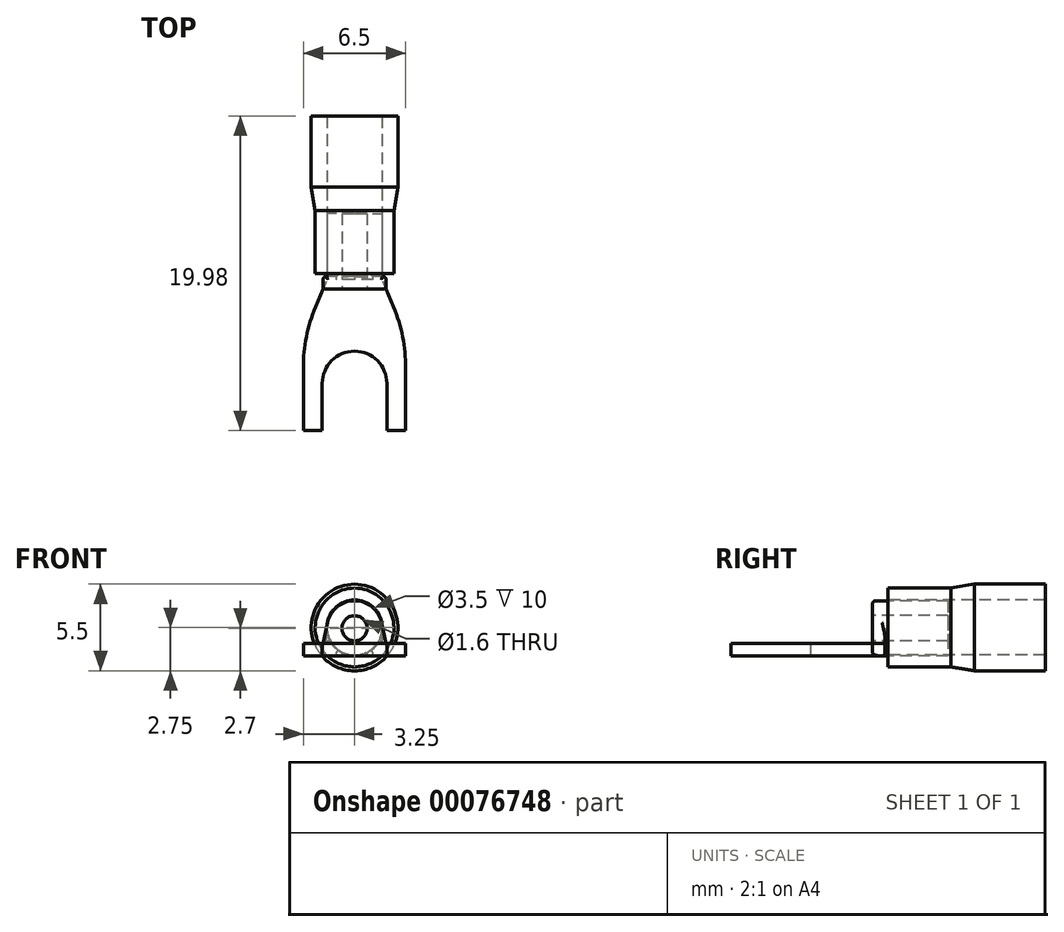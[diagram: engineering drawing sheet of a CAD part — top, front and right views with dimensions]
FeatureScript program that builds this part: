
annotation { "Feature Type Name" : "Feature", "Feature Type Description" : "" }
export const myFeature = defineFeature(function(context is Context, id is Id, definition is map)
    precondition{}
    {
        {
            var Q0;
            Q0=qCreatedBy(makeId("Top.planeOp"),FACE);
            var sketch = newSketch(context, id + "F0", { "sketchPlane" : qUnion([Q0])});
            skLineSegment(sketch, "E0.bottom", {"start": v(2, 4.52) * mm, "end": v(-2, 4.52) * mm});
            skLineSegment(sketch, "E0.top", {"start": v(3.25, -4.48) * mm, "end": v(2.05, -4.48) * mm});
            skLineSegment(sketch, "E0.left", {"start": v(3.25, -0.48) * mm, "end": v(3.25, -4.48) * mm});
            skLineSegment(sketch, "E0.right", {"start": v(-3.25, -0.48) * mm, "end": v(-3.25, -4.48) * mm});
            skPoint(sketch, "E0.middle", {"position": v(0, 0) * mm});
            skLineSegment(sketch, "E1", {"start": v(2.05, -4.48) * mm, "end": v(2.05, -1.48) * mm});
            skLineSegment(sketch, "E2", {"start": v(-2.05, -4.48) * mm, "end": v(-2.05, -1.48) * mm});
            skArc(sketch, "E3", {"start": v(-2.05, -1.48) * mm, "mid": v(0, 0.57) * mm, "end": v(2.05, -1.48) * mm});
            skLineSegment(sketch, "E4", {"start": v(-2.48, 3.37) * mm, "end": v(-2, 4.52) * mm});
            skLineSegment(sketch, "E5", {"start": v(2.48, 3.37) * mm, "end": v(2, 4.52) * mm});
            skLineSegment(sketch, "E6", {"start": v(0, -4.48) * mm, "end": v(0, 4.52) * mm, "construction": true});
            skPoint(sketch, "E6.endSnap0", {"position": v(0, 0.57) * mm});
            skLineSegment(sketch, "E7.trimOffspring", {"start": v(-2.05, -4.48) * mm, "end": v(-3.25, -4.48) * mm});
            skPoint(sketch, "E8.visualSharp", {"position": v(-3.25, 1.52) * mm});
            skArc(sketch, "E8.filletArc", {"start": v(-2.48, 3.37) * mm, "mid": v(-3.06, 1.48) * mm, "end": v(-3.25, -0.48) * mm});
            skPoint(sketch, "E9.visualSharp", {"position": v(3.25, 1.52) * mm});
            skArc(sketch, "E9.filletArc", {"start": v(3.25, -0.48) * mm, "mid": v(3.06, 1.48) * mm, "end": v(2.48, 3.37) * mm});
            skSolve(sketch);
        }
        {
            var Q0;
            Q0=qSketchRegion(id+"F0",true);
            extrude(context, id + "F1", {"entities" : qUnion([Q0]), "depth" : 0.8 * mm});
        }
        {
            var Q0;
            Q0=makeQuery(id+"F1.opExtrude","SWEPT_FACE",FACE,{"disambiguationData":[OSD([sQuery(id+"F0.wireOp",EDGE,"E0.bottom")])]});
            var sketch = newSketch(context, id + "F2", { "sketchPlane" : qUnion([Q0])});
            skCircle(sketch, "E10", {"center": v(0, 1.75) * mm, "radius": 0.8 * mm});
            skArc(sketch, "E11", {"start": v(1.7, 2.12) * mm, "mid": v(0, 3.5) * mm, "end": v(-1.7, 2.12) * mm});
            skLineSegment(sketch, "E12", {"start": v(-2, 0) * mm, "end": v(-2, 0.8) * mm});
            skLineSegment(sketch, "E13", {"start": v(-2, 0.8) * mm, "end": v(-1.7, 2.12) * mm});
            skLineSegment(sketch, "E14", {"start": v(2, 0) * mm, "end": v(2, 0.8) * mm});
            skLineSegment(sketch, "E15", {"start": v(2, 0.8) * mm, "end": v(1.7, 2.12) * mm});
            skLineSegment(sketch, "E16", {"start": v(-2, 0) * mm, "end": v(2, 0) * mm});
            skSolve(sketch);
        }
        {
            var Q0;
            Q0=qSketchRegion(id+"F2",true);
            extrude(context, id + "F3", {"entities" : qUnion([Q0]), "operationType" : NewBodyOperationType.ADD, "depth" : 0.8 * mm});
        }
        {
            var Q0;
            Q0=makeQuery(id+"F3.opExtrude","CAP_FACE",FACE,{"disambiguationData":[OSD([sQuery(id+"F2.wireOp",EDGE,"E10"),sQuery(id+"F2.wireOp",EDGE,"E11"),sQuery(id+"F2.wireOp",EDGE,"E12"),sQuery(id+"F2.wireOp",EDGE,"E13"),sQuery(id+"F2.wireOp",EDGE,"E14"),sQuery(id+"F2.wireOp",EDGE,"E15"),sQuery(id+"F2.wireOp",EDGE,"E16")])],"isStart":false});
            var sketch = newSketch(context, id + "F4", { "sketchPlane" : qUnion([Q0])});
            skCircle(sketch, "E17", {"center": v(0, 1.75) * mm, "radius": 1.75 * mm});
            skCircle(sketch, "E18", {"center": v(0, 1.75) * mm, "radius": 0.8 * mm});
            skSolve(sketch);
        }
        {
            var Q0;
            Q0=qSketchRegion(id+"F4",true);
            extrude(context, id + "F5", {"entities" : qUnion([Q0]), "operationType" : NewBodyOperationType.ADD, "depth" : 4 * mm});
        }
        {
            var Q0;
            {var subQ0=sQuery(id+"F2.wireOp",EDGE,"E13");var subQ3=sQuery(id+"F4.wireOp",EDGE,"E17");Q0=makeQuery(id+"F5.boolean.opBoolean","SPLIT",EDGE,{"disambiguationData":[TD([makeQuery(id+"F3.opExtrude","SWEPT_FACE",FACE,{"disambiguationData":[OSD([subQ0])]})])],"derivedFrom":makeQuery(id+"F5.opExtrude","CAP_EDGE",EDGE,{"disambiguationData":[OSD([subQ3])],"isStart":true})});}
            var Q1;
            {var subQ0=sQuery(id+"F2.wireOp",EDGE,"E15");var subQ3=sQuery(id+"F4.wireOp",EDGE,"E17");Q1=makeQuery(id+"F5.boolean.opBoolean","SPLIT",EDGE,{"disambiguationData":[TD([makeQuery(id+"F3.opExtrude","SWEPT_FACE",FACE,{"disambiguationData":[OSD([subQ0])]})])],"derivedFrom":makeQuery(id+"F5.opExtrude","CAP_EDGE",EDGE,{"disambiguationData":[OSD([subQ3])],"isStart":true})});}
            var Q2;
            Q2=makeQuery(id+"F3.opExtrude","CAP_EDGE",EDGE,{"disambiguationData":[OSD([sQuery(id+"F2.wireOp",EDGE,"E14")])],"isStart":false});
            var Q3;
            {var subQ0=sQuery(id+"F2.wireOp",EDGE,"E14");var subQ2=sQuery(id+"F2.wireOp",EDGE,"E16");Q3=makeQuery(id+"F5.boolean.opBoolean","SPLIT",EDGE,{"disambiguationData":[TD([makeQuery(id+"F3.opExtrude","SWEPT_FACE",FACE,{"disambiguationData":[OSD([subQ0])]})])],"derivedFrom":makeQuery(id+"F3.opExtrude","CAP_EDGE",EDGE,{"disambiguationData":[OSD([subQ2])],"isStart":false})});}
            var Q4;
            {var subQ0=sQuery(id+"F2.wireOp",EDGE,"E12");var subQ2=sQuery(id+"F2.wireOp",EDGE,"E16");Q4=makeQuery(id+"F5.boolean.opBoolean","SPLIT",EDGE,{"disambiguationData":[TD([makeQuery(id+"F3.opExtrude","SWEPT_FACE",FACE,{"disambiguationData":[OSD([subQ0])]})])],"derivedFrom":makeQuery(id+"F3.opExtrude","CAP_EDGE",EDGE,{"disambiguationData":[OSD([subQ2])],"isStart":false})});}
            var Q5;
            Q5=makeQuery(id+"F3.opExtrude","CAP_EDGE",EDGE,{"disambiguationData":[OSD([sQuery(id+"F2.wireOp",EDGE,"E12")])],"isStart":false});
            var Q6;
            Q6=makeQuery(id+"F3.opExtrude","CAP_EDGE",EDGE,{"disambiguationData":[OSD([sQuery(id+"F2.wireOp",EDGE,"E13")])],"isStart":false});
            var Q7;
            Q7=makeQuery(id+"F3.opExtrude","CAP_EDGE",EDGE,{"disambiguationData":[OSD([sQuery(id+"F2.wireOp",EDGE,"E15")])],"isStart":false});
            var Q8;
            Q8=makeQuery(id+"F3.opExtrude","SWEPT_EDGE",EDGE,{"disambiguationData":[OSD([sQuery(id+"F2.wireOp",EDGE,"E14"),sQuery(id+"F2.wireOp",EDGE,"E16")])]});
            var Q9;
            Q9=makeQuery(id+"F3.opExtrude","SWEPT_EDGE",EDGE,{"disambiguationData":[OSD([sQuery(id+"F2.wireOp",EDGE,"E12"),sQuery(id+"F2.wireOp",EDGE,"E16")])]});
            var Q10;
            Q10=makeQuery(id+"F3.opExtrude","CAP_EDGE",EDGE,{"disambiguationData":[OSD([sQuery(id+"F2.wireOp",EDGE,"E13")])],"isStart":true});
            var Q11;
            Q11=makeQuery(id+"F3.opExtrude","CAP_EDGE",EDGE,{"disambiguationData":[OSD([sQuery(id+"F2.wireOp",EDGE,"E11")])],"isStart":true});
            fillet(context, id + "F6", {"entities" : qUnion([Q0, Q1, Q2, Q3, Q4, Q5, Q6, Q7, Q8, Q9, Q10, Q11]), "radius" : 0.2 * mm, "tangentPropagation" : true, "allowEdgeOverflow" : false});
        }
        {
            var Q0;
            Q0=makeQuery(id+"F1.opExtrude","CAP_FACE",FACE,{"disambiguationData":[OSD([sQuery(id+"F0.wireOp",EDGE,"E0.bottom"),sQuery(id+"F0.wireOp",EDGE,"E0.top"),sQuery(id+"F0.wireOp",EDGE,"E0.left"),sQuery(id+"F0.wireOp",EDGE,"E0.right"),sQuery(id+"F0.wireOp",EDGE,"E1"),sQuery(id+"F0.wireOp",EDGE,"E2"),sQuery(id+"F0.wireOp",EDGE,"E3"),sQuery(id+"F0.wireOp",EDGE,"E4"),sQuery(id+"F0.wireOp",EDGE,"E5"),sQuery(id+"F0.wireOp",EDGE,"E7.trimOffspring"),sQuery(id+"F0.wireOp",EDGE,"E8.filletArc"),sQuery(id+"F0.wireOp",EDGE,"E9.filletArc")])],"isStart":false});
            cPlane(context, id + "F7", {"entities" : qUnion([Q0]), "cplaneType" : CPlaneType.OFFSET, "offset" : 1 * mm, "width" : 150 * mm, "height" : 150 * mm});
        }
        {
            var Q0;
            Q0=qCreatedBy(id+"F7.planeOp",FACE);
            var sketch = newSketch(context, id + "F8", { "sketchPlane" : qUnion([Q0])});
            skLineSegment(sketch, "E19", {"start": v(0, 5.5) * mm, "end": v(0, 15.5) * mm, "construction": true});
            skLineSegment(sketch, "E20", {"start": v(-1.75, 5.5) * mm, "end": v(-1.75, 15.5) * mm});
            skLineSegment(sketch, "E21", {"start": v(-1.75, 15.5) * mm, "end": v(-2.75, 15.5) * mm});
            skLineSegment(sketch, "E22", {"start": v(-2.75, 15.5) * mm, "end": v(-2.75, 11) * mm});
            skLineSegment(sketch, "E23", {"start": v(-2.5, 9.5) * mm, "end": v(-2.5, 5.5) * mm});
            skLineSegment(sketch, "E24", {"start": v(-2.5, 5.5) * mm, "end": v(-1.75, 5.5) * mm});
            skLineSegment(sketch, "E25", {"start": v(-2.75, 11) * mm, "end": v(-2.5, 9.5) * mm});
            skSolve(sketch);
        }
        {
            var Q0;
            Q0=qSketchRegion(id+"F8",true);
            var Q1;
            Q1=sQuery(id+"F8.wireOp",EDGE,"E19");
            revolve(context, id + "F9", {"entities" : qUnion([Q0]), "axis" : qUnion([Q1]), "revolveType" : RevolveType.FULL});
        }
    });
